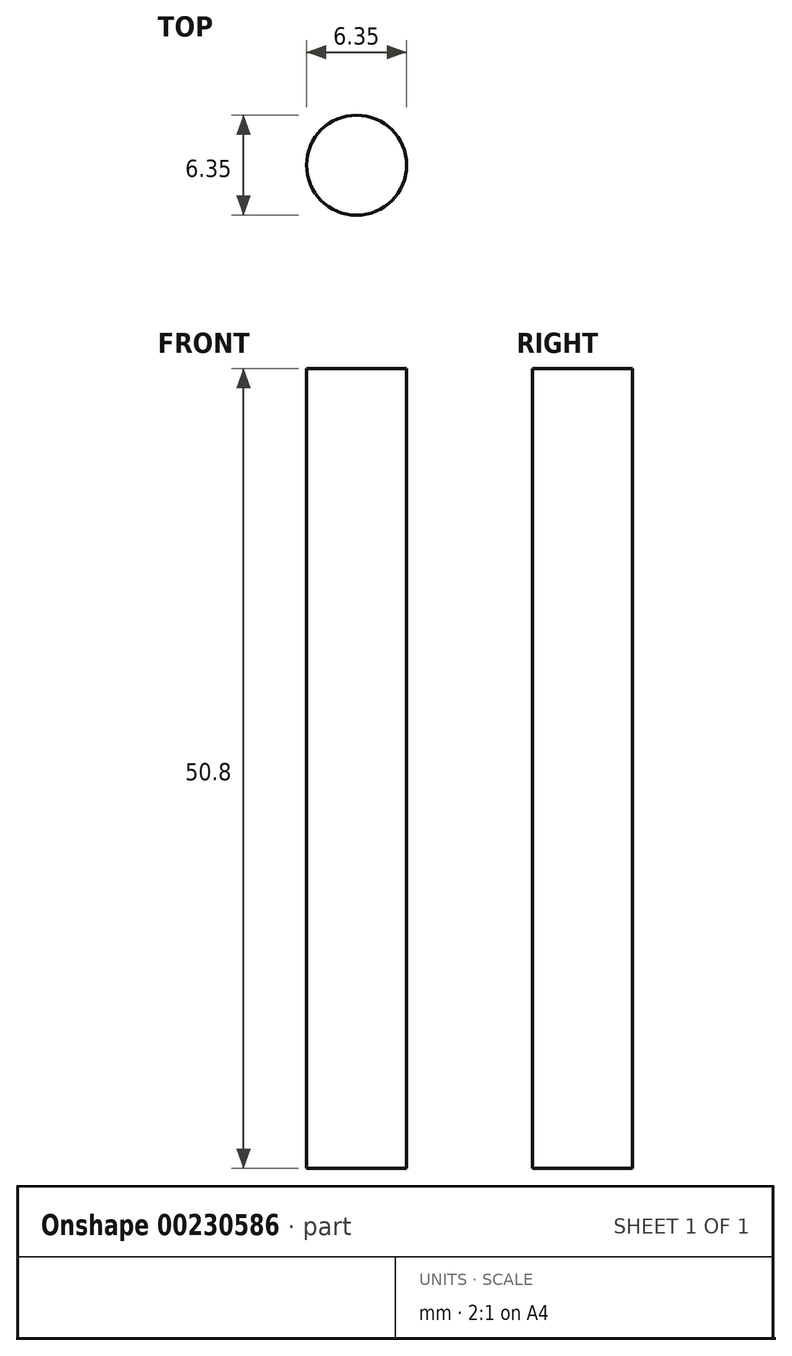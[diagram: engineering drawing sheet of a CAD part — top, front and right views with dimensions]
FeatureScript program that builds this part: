
annotation { "Feature Type Name" : "Feature", "Feature Type Description" : "" }
export const myFeature = defineFeature(function(context is Context, id is Id, definition is map)
    precondition{}
    {
        {
            var Q0;
            Q0=qCreatedBy(makeId("Top.planeOp"),FACE);
            var sketch = newSketch(context, id + "F0", { "sketchPlane" : qUnion([Q0])});
            skCircle(sketch, "E0", {"center": v(24.4, -30.1) * mm, "radius": 3.17 * mm});
            skSolve(sketch);
        }
        {
            var Q0;
            Q0=makeQuery(id+"F0.imprint","IMPRINT",FACE,{"disambiguationData":[TD([[makeQuery(id+"F0.imprint","IMPRINT",EDGE,{"derivedFrom":sQuery(id+"F0.wireOp",EDGE,"E0")}),1.0]])]});
            extrude(context, id + "F1", {"entities" : qUnion([Q0]), "depth" : 50.8 * mm});
        }
    });
